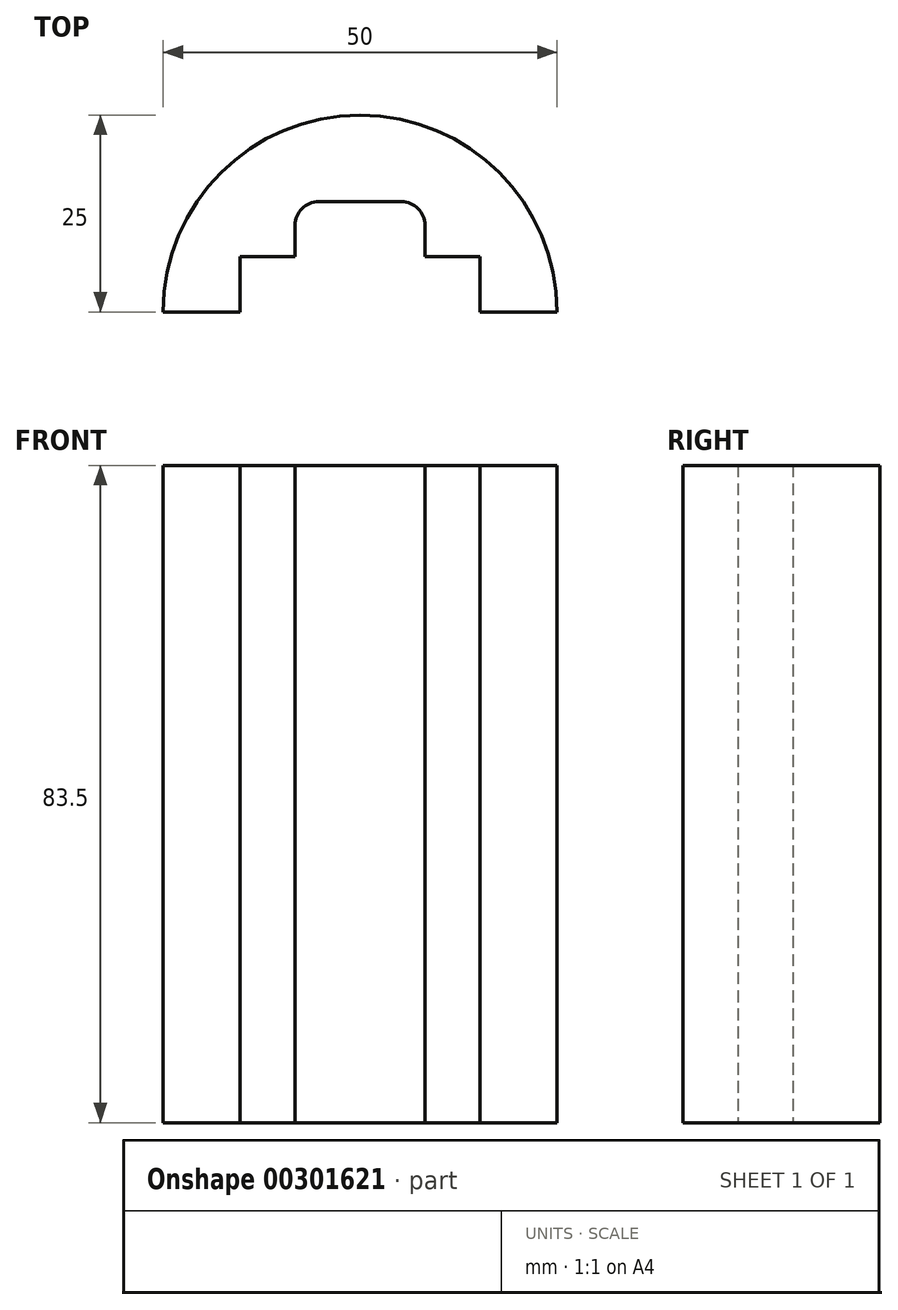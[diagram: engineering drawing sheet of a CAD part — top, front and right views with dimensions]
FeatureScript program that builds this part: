
annotation { "Feature Type Name" : "Feature", "Feature Type Description" : "" }
export const myFeature = defineFeature(function(context is Context, id is Id, definition is map)
    precondition{}
    {
        {
            var Q0;
            Q0=qCreatedBy(makeId("Top.planeOp"),FACE);
            var sketch = newSketch(context, id + "F0", { "sketchPlane" : qUnion([Q0])});
            skLineSegment(sketch, "E0", {"start": v(-15.25, -7) * mm, "end": v(-15.25, 0) * mm});
            skLineSegment(sketch, "E1", {"start": v(-15.25, 0) * mm, "end": v(-8.25, 0) * mm});
            skLineSegment(sketch, "E2", {"start": v(-8.25, 0) * mm, "end": v(-8.25, 7) * mm});
            skLineSegment(sketch, "E3", {"start": v(-8.25, 7) * mm, "end": v(0, 7) * mm});
            skArc(sketch, "E4", {"start": v(-25, -7) * mm, "mid": v(-17.68, 10.68) * mm, "end": v(0, 18) * mm});
            skArc(sketch, "E5", {"start": v(0, 23) * mm, "mid": v(-21.21, 14.21) * mm, "end": v(-30, -7) * mm});
            skLineSegment(sketch, "E6", {"start": v(-15.25, -7) * mm, "end": v(-30, -7) * mm});
            skLineSegment(sketch, "E7", {"start": v(0, 23) * mm, "end": v(0, 7) * mm});
            skSolve(sketch);
        }
        {
            var Q0;
            {var subQ1=sQuery(id+"F0.wireOp",EDGE,"E0");Q0=makeQuery(id+"F0.imprint","IMPRINT",FACE,{"disambiguationData":[TD([[makeQuery(id+"F0.imprint","IMPRINT",EDGE,{"derivedFrom":subQ1}),1.0]])]});}
            extrude(context, id + "F1", {"entities" : qUnion([Q0]), "endBound" : BoundingType.SYMMETRIC, "depth" : 83.5 * mm});
        }
        {
            var Q0;
            {var subQ0=sQuery(id+"F0.wireOp",EDGE,"E4");Q0=makeQuery(id+"F0.imprint","IMPRINT",FACE,{"disambiguationData":[TD([[makeQuery(id+"F0.imprint","IMPRINT",EDGE,{"derivedFrom":subQ0}),1.0]])]});}
            var Q1;
            Q1=makeQuery(id+"F1.opExtrude","CAP_FACE",FACE,{"disambiguationData":[OSD([sQuery(id+"F0.wireOp",EDGE,"E0"),sQuery(id+"F0.wireOp",EDGE,"E1"),sQuery(id+"F0.wireOp",EDGE,"E2"),sQuery(id+"F0.wireOp",EDGE,"E3"),sQuery(id+"F0.wireOp",EDGE,"E4"),sQuery(id+"F0.wireOp",EDGE,"E6"),sQuery(id+"F0.wireOp",EDGE,"E7")])],"isStart":true});
            extrude(context, id + "F2", {"entities" : qUnion([Q0]), "operationType" : NewBodyOperationType.ADD, "endBound" : BoundingType.UP_TO_SURFACE, "oppositeDirection" : true, "endBoundEntityFace" : qUnion([Q1]), "depth" : 40 * mm, "hasSecondDirection" : true, "secondDirectionOppositeDirection" : true, "secondDirectionDepth" : 38 * mm});
        }
        {
            var Q0;
            Q0=makeQuery(id+"F1.opExtrude","SWEPT_EDGE",EDGE,{"disambiguationData":[OSD([sQuery(id+"F0.wireOp",EDGE,"E2"),sQuery(id+"F0.wireOp",EDGE,"E3")])]});
            var Q1;
            Q1=makeQuery(id+"F2.opExtrude","CAP_EDGE",EDGE,{"disambiguationData":[OSD([sQuery(id+"F0.wireOp",EDGE,"E4")])],"isStart":true});
            fillet(context, id + "F3", {"entities" : qUnion([Q0, Q1]), "radius" : 3 * mm, "tangentPropagation" : true, "allowEdgeOverflow" : false});
        }
        {
            var Q0;
            Q0=makeQuery(id+"F1.opExtrude","SWEPT_BODY",BODY,{"disambiguationData":[OSD([sQuery(id+"F0.wireOp",EDGE,"E0"),sQuery(id+"F0.wireOp",EDGE,"E1"),sQuery(id+"F0.wireOp",EDGE,"E2"),sQuery(id+"F0.wireOp",EDGE,"E3"),sQuery(id+"F0.wireOp",EDGE,"E4"),sQuery(id+"F0.wireOp",EDGE,"E6"),sQuery(id+"F0.wireOp",EDGE,"E7")])]});
            var Q1;
            Q1=qCreatedBy(makeId("Right.planeOp"),FACE);
            mirror(context, id + "F4", {"operationType" : NewBodyOperationType.ADD, "entities" : qUnion([Q0]), "mirrorPlane" : qUnion([Q1])});
        }
    });
